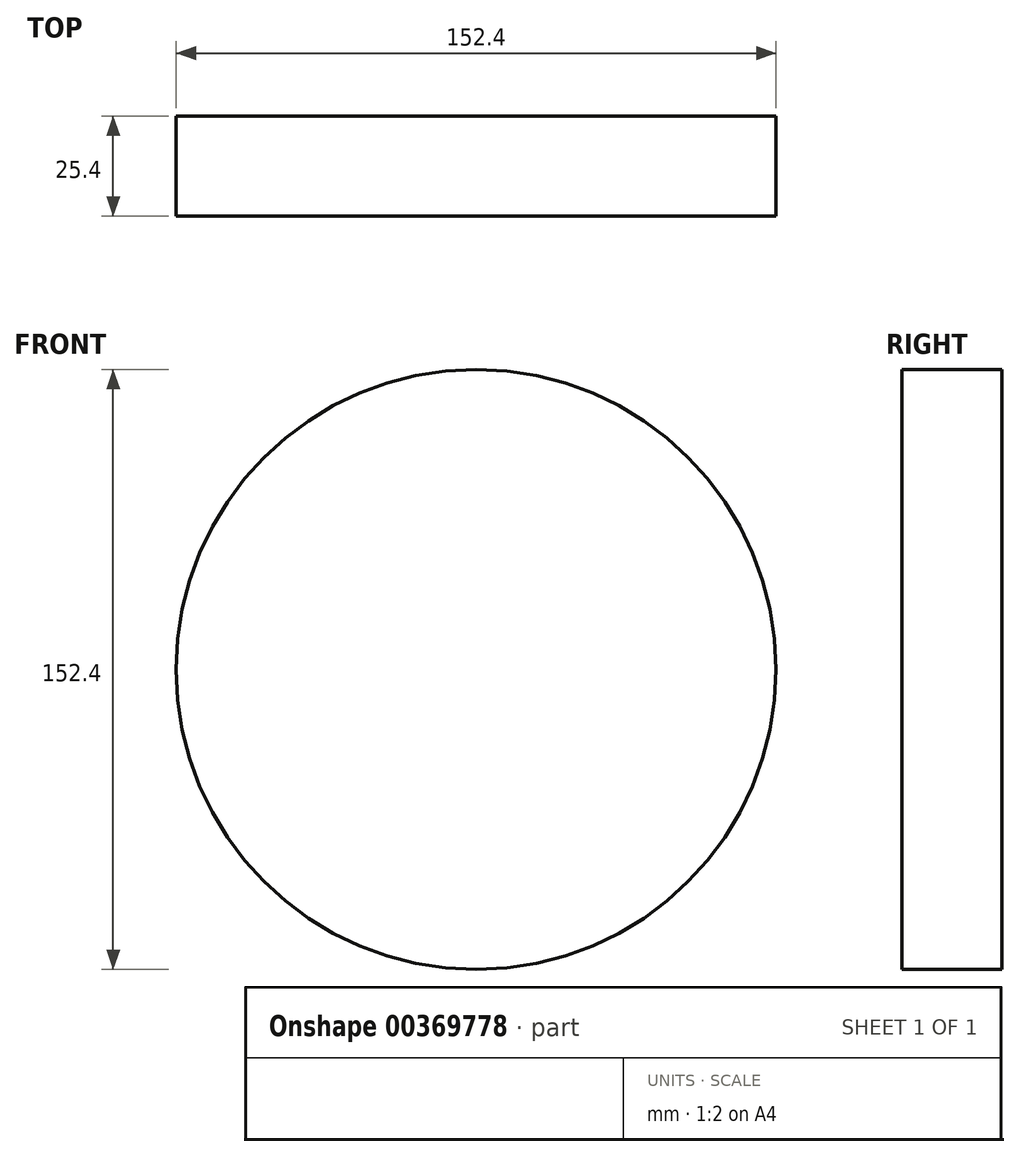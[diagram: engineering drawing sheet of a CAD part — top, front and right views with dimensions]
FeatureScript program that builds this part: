
annotation { "Feature Type Name" : "Feature", "Feature Type Description" : "" }
export const myFeature = defineFeature(function(context is Context, id is Id, definition is map)
    precondition{}
    {
        {
            var Q0;
            Q0=qCreatedBy(makeId("Front.planeOp"),FACE);
            var sketch = newSketch(context, id + "F0", { "sketchPlane" : qUnion([Q0])});
            skCircle(sketch, "E0", {"center": v(0, 0) * mm, "radius": 76.2 * mm});
            skSolve(sketch);
        }
        {
            var Q0;
            Q0=makeQuery(id+"F0.imprint","IMPRINT",FACE,{"disambiguationData":[TD([[makeQuery(id+"F0.imprint","IMPRINT",EDGE,{"derivedFrom":sQuery(id+"F0.wireOp",EDGE,"E0")}),1.0]])]});
            extrude(context, id + "F1", {"entities" : qUnion([Q0]), "depth" : 25.4 * mm});
        }
    });
